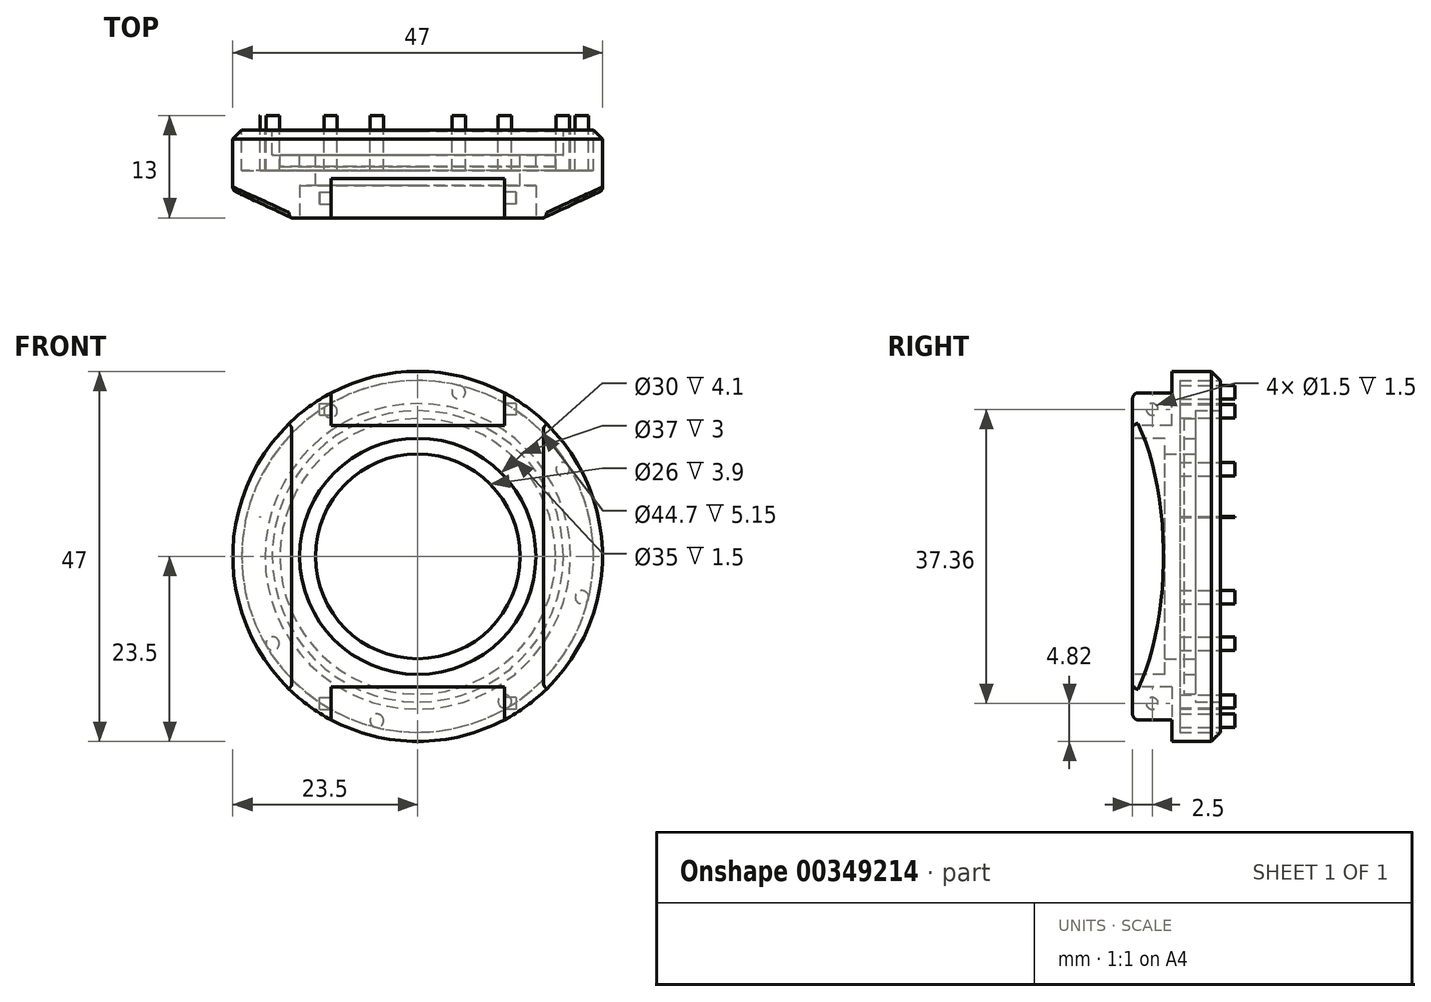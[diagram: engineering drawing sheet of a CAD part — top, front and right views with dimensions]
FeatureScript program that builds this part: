
annotation { "Feature Type Name" : "Feature", "Feature Type Description" : "" }
export const myFeature = defineFeature(function(context is Context, id is Id, definition is map)
    precondition{}
    {
        {
            var Q0;
            Q0=qCreatedBy(makeId("Front.planeOp"),FACE);
            var sketch = newSketch(context, id + "F0", { "sketchPlane" : qUnion([Q0])});
            skCircle(sketch, "E0", {"center": v(0, 0) * mm, "radius": 23.5 * mm});
            skCircle(sketch, "E1", {"center": v(0, 0) * mm, "radius": 15 * mm});
            skLineSegment(sketch, "E2", {"start": v(11, 16.6) * mm, "end": v(11, 20.77) * mm});
            skLineSegment(sketch, "E3", {"start": v(-11, 16.6) * mm, "end": v(11, 16.6) * mm});
            skLineSegment(sketch, "E4.MirrorCS", {"start": v(-11, -16.6) * mm, "end": v(11, -16.6) * mm});
            skLineSegment(sketch, "E5", {"start": v(16, -17.21) * mm, "end": v(16, 17.21) * mm});
            skLineSegment(sketch, "E6.MirrorCS", {"start": v(-16, -17.21) * mm, "end": v(-16, 17.21) * mm});
            skLineSegment(sketch, "E7", {"start": v(-11, -16.6) * mm, "end": v(-11, -20.77) * mm});
            skLineSegment(sketch, "E8", {"start": v(11, -16.6) * mm, "end": v(11, -20.77) * mm});
            skLineSegment(sketch, "E9", {"start": v(-11, 16.6) * mm, "end": v(-11, 20.77) * mm});
            skSolve(sketch);
        }
        {
            var Q0;
            Q0=makeQuery(id+"F0.imprint","IMPRINT",FACE,{"disambiguationData":[TD([[makeQuery(id+"F0.imprint","IMPRINT",EDGE,{"derivedFrom":sQuery(id+"F0.wireOp",EDGE,"E1")}),-1.0]])]});
            var Q1;
            {var subQ0=sQuery(id+"F0.wireOp",EDGE,"E2");Q1=makeQuery(id+"F0.imprint","IMPRINT",FACE,{"disambiguationData":[TD([[makeQuery(id+"F0.imprint","IMPRINT",EDGE,{"derivedFrom":subQ0}),1.0]])]});}
            var Q2;
            {var subQ0=sQuery(id+"F0.wireOp",EDGE,"5be4e37a-e5fa-453b-b9c4-1bad559851300.MirrorCS");Q2=makeQuery(id+"F0.imprint","IMPRINT",FACE,{"disambiguationData":[TD([[makeQuery(id+"F0.imprint","IMPRINT",EDGE,{"derivedFrom":subQ0}),1.0]])]});}
            var Q3;
            {var subQ0=sQuery(id+"F0.wireOp",EDGE,"E6.MirrorCS");Q3=makeQuery(id+"F0.imprint","IMPRINT",FACE,{"disambiguationData":[TD([[makeQuery(id+"F0.imprint","IMPRINT",EDGE,{"derivedFrom":subQ0}),1.0]])]});}
            var Q4;
            {var subQ0=sQuery(id+"F0.wireOp",EDGE,"E5");Q4=makeQuery(id+"F0.imprint","IMPRINT",FACE,{"disambiguationData":[TD([[makeQuery(id+"F0.imprint","IMPRINT",EDGE,{"derivedFrom":subQ0}),-1.0]])]});}
            var Q5;
            Q5=makeQuery(id+"F0.imprint","IMPRINT",FACE,{"disambiguationData":[TD([[makeQuery(id+"F0.imprint","IMPRINT",EDGE,{"derivedFrom":sQuery(id+"F0.wireOp",EDGE,"E1")}),1.0]])]});
            var Q6;
            Q6=makeQuery(id+"F0.imprint","IMPRINT",FACE,{"disambiguationData":[TD([[makeQuery(id+"F0.imprint","IMPRINT",EDGE,{"derivedFrom":sQuery(id+"F0.wireOp",EDGE,"E4.MirrorCS")}),-1.0]])]});
            extrude(context, id + "F1", {"entities" : qUnion([Q0, Q1, Q2, Q3, Q4, Q5, Q6]), "oppositeDirection" : true, "depth" : 13 * mm});
        }
        {
            var Q0;
            {var subQ0=sQuery(id+"F0.wireOp",EDGE,"E2");Q0=makeQuery(id+"F0.imprint","IMPRINT",FACE,{"disambiguationData":[TD([[makeQuery(id+"F0.imprint","IMPRINT",EDGE,{"derivedFrom":subQ0}),1.0]])]});}
            var Q1;
            Q1=makeQuery(id+"F0.imprint","IMPRINT",FACE,{"disambiguationData":[TD([[makeQuery(id+"F0.imprint","IMPRINT",EDGE,{"derivedFrom":sQuery(id+"F0.wireOp",EDGE,"E4.MirrorCS")}),-1.0]])]});
            extrude(context, id + "F2", {"entities" : qUnion([Q0, Q1]), "operationType" : NewBodyOperationType.REMOVE, "oppositeDirection" : true, "depth" : 5 * mm});
        }
        {
            var Q0;
            Q0=makeQuery(id+"F0.imprint","IMPRINT",FACE,{"disambiguationData":[TD([[makeQuery(id+"F0.imprint","IMPRINT",EDGE,{"derivedFrom":sQuery(id+"F0.wireOp",EDGE,"E1")}),1.0]])]});
            extrude(context, id + "F3", {"entities" : qUnion([Q0]), "operationType" : NewBodyOperationType.REMOVE, "oppositeDirection" : true, "depth" : 4.1 * mm});
        }
        {
            var Q0;
            Q0=makeQuery(id+"F1.opExtrude","CAP_FACE",FACE,{"disambiguationData":[OSD([sQuery(id+"F0.wireOp",EDGE,"E0")])],"isStart":false});
            var sketch = newSketch(context, id + "F4", { "sketchPlane" : qUnion([Q0])});
            skCircle(sketch, "E10", {"center": v(0, 0) * mm, "radius": 19.4 * mm});
            skSolve(sketch);
        }
        {
            var Q0;
            Q0=makeQuery(id+"F4.imprint","IMPRINT",FACE,{"disambiguationData":[TD([[makeQuery(id+"F4.imprint","IMPRINT",EDGE,{"derivedFrom":sQuery(id+"F4.wireOp",EDGE,"E10")}),1.0]])]});
            extrude(context, id + "F5", {"entities" : qUnion([Q0]), "operationType" : NewBodyOperationType.REMOVE, "oppositeDirection" : true, "depth" : 2 * mm});
        }
        {
            var Q0;
            Q0=qCreatedBy(makeId("Top.planeOp"),FACE);
            var sketch = newSketch(context, id + "F6", { "sketchPlane" : qUnion([Q0])});
            skLineSegment(sketch, "E11", {"start": v(0, 0) * mm, "end": v(0, 13) * mm});
            skLineSegment(sketch, "E12", {"start": v(16, 0) * mm, "end": v(30.1, 6.57) * mm});
            skLineSegment(sketch, "E13", {"start": v(30.1, 6.57) * mm, "end": v(30.1, 0) * mm});
            skLineSegment(sketch, "E14", {"start": v(30.1, 0) * mm, "end": v(16, 0) * mm});
            skLineSegment(sketch, "E15.MirrorCS", {"start": v(-16, 0) * mm, "end": v(-30.1, 6.57) * mm});
            skLineSegment(sketch, "E16.MirrorCS", {"start": v(-30.1, 0) * mm, "end": v(-16, 0) * mm});
            skLineSegment(sketch, "E17.MirrorCS", {"start": v(-30.1, 6.57) * mm, "end": v(-30.1, 0) * mm});
            skSolve(sketch);
        }
        {
            var Q0;
            Q0=makeQuery(id+"F6.imprint","IMPRINT",FACE,{"disambiguationData":[TD([[makeQuery(id+"F6.imprint","IMPRINT",EDGE,{"derivedFrom":sQuery(id+"F6.wireOp",EDGE,"E15.MirrorCS")}),1.0]])]});
            var Q1;
            Q1=makeQuery(id+"F6.imprint","IMPRINT",FACE,{"disambiguationData":[TD([[makeQuery(id+"F6.imprint","IMPRINT",EDGE,{"derivedFrom":sQuery(id+"F6.wireOp",EDGE,"E12")}),-1.0]])]});
            extrude(context, id + "F7", {"entities" : qUnion([Q0, Q1]), "operationType" : NewBodyOperationType.REMOVE, "oppositeDirection" : true, "depth" : 30 * mm});
        }
        {
            var Q0;
            Q0=makeQuery(id+"F7.boolean.opBoolean","COPY",FACE,{"derivedFrom":makeQuery(id+"F7.opExtrude","CAP_FACE",FACE,{"disambiguationData":[OSD([sQuery(id+"F6.wireOp",EDGE,"E12"),sQuery(id+"F6.wireOp",EDGE,"E13"),sQuery(id+"F6.wireOp",EDGE,"E14")])],"isStart":true})});
            var Q1;
            Q1=makeQuery(id+"F7.boolean.opBoolean","COPY",FACE,{"derivedFrom":makeQuery(id+"F7.opExtrude","CAP_FACE",FACE,{"disambiguationData":[OSD([sQuery(id+"F6.wireOp",EDGE,"E15.MirrorCS"),sQuery(id+"F6.wireOp",EDGE,"E16.MirrorCS"),sQuery(id+"F6.wireOp",EDGE,"E17.MirrorCS")])],"isStart":true})});
            extrude(context, id + "F8", {"entities" : qUnion([Q0, Q1]), "operationType" : NewBodyOperationType.REMOVE, "oppositeDirection" : true, "depth" : 30 * mm});
        }
        {
            var Q0;
            Q0=makeQuery(id+"F8.boolean.opBoolean","INTERSECT",EDGE,{"derivedFrom":[makeQuery(id+"F1.opExtrude","SWEPT_FACE",FACE,{"disambiguationData":[OSD([sQuery(id+"F0.wireOp",EDGE,"E0")])]}),makeQuery(id+"F8.opExtrude","SWEPT_FACE",FACE,{"disambiguationData":[OSD([sQuery(id+"F6.wireOp",EDGE,"E15.MirrorCS")])]})]});
            var Q1;
            {var subQ0=sQuery(id+"F0.wireOp",EDGE,"E0");var subQ2=makeQuery(id+"F2.opExtrude","SWEPT_FACE",FACE,{"disambiguationData":[OSD([sQuery(id+"F0.wireOp",EDGE,"bd44ebf7-4620-4fe3-8905-c25fbdf720250.MirrorCS")])]});Q1=makeQuery(id+"F7.boolean.opBoolean","SPLIT",EDGE,{"disambiguationData":[TD([makeQuery(id+"F2.boolean.opBoolean","COPY",FACE,{"derivedFrom":subQ2})])],"derivedFrom":makeQuery(id+"F2.boolean.opBoolean","SPLIT",EDGE,{"disambiguationData":[TD([subQ2])],"derivedFrom":makeQuery(id+"F1.opExtrude","CAP_EDGE",EDGE,{"disambiguationData":[OSD([subQ0])],"isStart":true})})});}
            var Q2;
            {var subQ0=sQuery(id+"F0.wireOp",EDGE,"E0");var subQ3=makeQuery(id+"F2.opExtrude","SWEPT_FACE",FACE,{"disambiguationData":[OSD([sQuery(id+"F0.wireOp",EDGE,"E2")])]});Q2=makeQuery(id+"F7.boolean.opBoolean","SPLIT",EDGE,{"disambiguationData":[TD([makeQuery(id+"F2.boolean.opBoolean","COPY",FACE,{"derivedFrom":subQ3})])],"derivedFrom":makeQuery(id+"F2.boolean.opBoolean","SPLIT",EDGE,{"disambiguationData":[TD([subQ3])],"derivedFrom":makeQuery(id+"F1.opExtrude","CAP_EDGE",EDGE,{"disambiguationData":[OSD([subQ0])],"isStart":true})})});}
            var Q3;
            Q3=makeQuery(id+"F8.boolean.opBoolean","INTERSECT",EDGE,{"derivedFrom":[makeQuery(id+"F1.opExtrude","SWEPT_FACE",FACE,{"disambiguationData":[OSD([sQuery(id+"F0.wireOp",EDGE,"E0")])]}),makeQuery(id+"F8.opExtrude","SWEPT_FACE",FACE,{"disambiguationData":[OSD([sQuery(id+"F6.wireOp",EDGE,"E12")])]})]});
            var Q4;
            {var subQ0=sQuery(id+"F0.wireOp",EDGE,"E0");var subQ3=makeQuery(id+"F2.opExtrude","SWEPT_FACE",FACE,{"disambiguationData":[OSD([sQuery(id+"F0.wireOp",EDGE,"214ce4b7-124c-478d-bf7d-9a589a4742c70.MirrorCS")])]});Q4=makeQuery(id+"F7.boolean.opBoolean","SPLIT",EDGE,{"disambiguationData":[TD([makeQuery(id+"F2.boolean.opBoolean","COPY",FACE,{"derivedFrom":subQ3})])],"derivedFrom":makeQuery(id+"F2.boolean.opBoolean","SPLIT",EDGE,{"disambiguationData":[TD([makeQuery(id+"F2.opExtrude","SWEPT_FACE",FACE,{"disambiguationData":[OSD([sQuery(id+"F0.wireOp",EDGE,"E2")])]})])],"derivedFrom":makeQuery(id+"F1.opExtrude","CAP_EDGE",EDGE,{"disambiguationData":[OSD([subQ0])],"isStart":true})})});}
            var Q5;
            {var subQ0=sQuery(id+"F0.wireOp",EDGE,"E0");var subQ3=makeQuery(id+"F2.opExtrude","SWEPT_FACE",FACE,{"disambiguationData":[OSD([sQuery(id+"F0.wireOp",EDGE,"5be4e37a-e5fa-453b-b9c4-1bad559851300.MirrorCS")])]});Q5=makeQuery(id+"F7.boolean.opBoolean","SPLIT",EDGE,{"disambiguationData":[TD([makeQuery(id+"F2.boolean.opBoolean","COPY",FACE,{"derivedFrom":subQ3})])],"derivedFrom":makeQuery(id+"F2.boolean.opBoolean","SPLIT",EDGE,{"disambiguationData":[TD([makeQuery(id+"F2.opExtrude","SWEPT_FACE",FACE,{"disambiguationData":[OSD([sQuery(id+"F0.wireOp",EDGE,"bd44ebf7-4620-4fe3-8905-c25fbdf720250.MirrorCS")])]})])],"derivedFrom":makeQuery(id+"F1.opExtrude","CAP_EDGE",EDGE,{"disambiguationData":[OSD([subQ0])],"isStart":true})})});}
            var Q6;
            {var subQ0=sQuery(id+"F0.wireOp",EDGE,"E0");var subQ3=makeQuery(id+"F2.opExtrude","SWEPT_FACE",FACE,{"disambiguationData":[OSD([sQuery(id+"F0.wireOp",EDGE,"5be4e37a-e5fa-453b-b9c4-1bad559851300.MirrorCS")])]});Q6=makeQuery(id+"F7.boolean.opBoolean","SPLIT",EDGE,{"disambiguationData":[TD([makeQuery(id+"F2.boolean.opBoolean","COPY",FACE,{"derivedFrom":subQ3})])],"derivedFrom":makeQuery(id+"F2.boolean.opBoolean","SPLIT",EDGE,{"disambiguationData":[TD([subQ3])],"derivedFrom":makeQuery(id+"F1.opExtrude","CAP_EDGE",EDGE,{"disambiguationData":[OSD([subQ0])],"isStart":true})})});}
            var Q7;
            {var subQ0=sQuery(id+"F0.wireOp",EDGE,"E0");var subQ3=makeQuery(id+"F2.opExtrude","SWEPT_FACE",FACE,{"disambiguationData":[OSD([sQuery(id+"F0.wireOp",EDGE,"b6f2e5ea-f2be-490d-98a8-a135f803b0b40.MirrorCS")])]});Q7=makeQuery(id+"F7.boolean.opBoolean","SPLIT",EDGE,{"disambiguationData":[TD([makeQuery(id+"F2.boolean.opBoolean","COPY",FACE,{"derivedFrom":subQ3})])],"derivedFrom":makeQuery(id+"F2.boolean.opBoolean","SPLIT",EDGE,{"disambiguationData":[TD([makeQuery(id+"F2.opExtrude","SWEPT_FACE",FACE,{"disambiguationData":[OSD([sQuery(id+"F0.wireOp",EDGE,"5be4e37a-e5fa-453b-b9c4-1bad559851300.MirrorCS")])]})])],"derivedFrom":makeQuery(id+"F1.opExtrude","CAP_EDGE",EDGE,{"disambiguationData":[OSD([subQ0])],"isStart":true})})});}
            var Q8;
            {var subQ0=sQuery(id+"F0.wireOp",EDGE,"E0");var subQ3=makeQuery(id+"F2.opExtrude","SWEPT_FACE",FACE,{"disambiguationData":[OSD([sQuery(id+"F0.wireOp",EDGE,"b6f2e5ea-f2be-490d-98a8-a135f803b0b40.MirrorCS")])]});Q8=makeQuery(id+"F7.boolean.opBoolean","SPLIT",EDGE,{"disambiguationData":[TD([makeQuery(id+"F2.boolean.opBoolean","COPY",FACE,{"derivedFrom":subQ3})])],"derivedFrom":makeQuery(id+"F2.boolean.opBoolean","SPLIT",EDGE,{"disambiguationData":[TD([subQ3])],"derivedFrom":makeQuery(id+"F1.opExtrude","CAP_EDGE",EDGE,{"disambiguationData":[OSD([subQ0])],"isStart":true})})});}
            var Q9;
            {var subQ0=sQuery(id+"F0.wireOp",EDGE,"E0");var subQ3=makeQuery(id+"F2.opExtrude","SWEPT_FACE",FACE,{"disambiguationData":[OSD([sQuery(id+"F0.wireOp",EDGE,"E7")])]});Q9=makeQuery(id+"F7.boolean.opBoolean","SPLIT",EDGE,{"disambiguationData":[TD([makeQuery(id+"F2.boolean.opBoolean","COPY",FACE,{"derivedFrom":subQ3})])],"derivedFrom":makeQuery(id+"F2.boolean.opBoolean","SPLIT",EDGE,{"disambiguationData":[TD([makeQuery(id+"F2.opExtrude","SWEPT_FACE",FACE,{"disambiguationData":[OSD([sQuery(id+"F0.wireOp",EDGE,"b6f2e5ea-f2be-490d-98a8-a135f803b0b40.MirrorCS")])]})])],"derivedFrom":makeQuery(id+"F1.opExtrude","CAP_EDGE",EDGE,{"disambiguationData":[OSD([subQ0])],"isStart":true})})});}
            var Q10;
            {var subQ0=sQuery(id+"F0.wireOp",EDGE,"E0");var subQ3=makeQuery(id+"F2.opExtrude","SWEPT_FACE",FACE,{"disambiguationData":[OSD([sQuery(id+"F0.wireOp",EDGE,"E8")])]});Q10=makeQuery(id+"F7.boolean.opBoolean","SPLIT",EDGE,{"disambiguationData":[TD([makeQuery(id+"F2.boolean.opBoolean","COPY",FACE,{"derivedFrom":subQ3})])],"derivedFrom":makeQuery(id+"F2.boolean.opBoolean","SPLIT",EDGE,{"disambiguationData":[TD([makeQuery(id+"F2.opExtrude","SWEPT_FACE",FACE,{"disambiguationData":[OSD([sQuery(id+"F0.wireOp",EDGE,"E2")])]})])],"derivedFrom":makeQuery(id+"F1.opExtrude","CAP_EDGE",EDGE,{"disambiguationData":[OSD([subQ0])],"isStart":true})})});}
            var Q11;
            {var subQ0=sQuery(id+"F0.wireOp",EDGE,"E0");var subQ3=makeQuery(id+"F2.opExtrude","SWEPT_FACE",FACE,{"disambiguationData":[OSD([sQuery(id+"F0.wireOp",EDGE,"E9")])]});Q11=makeQuery(id+"F7.boolean.opBoolean","SPLIT",EDGE,{"disambiguationData":[TD([makeQuery(id+"F2.boolean.opBoolean","COPY",FACE,{"derivedFrom":subQ3})])],"derivedFrom":makeQuery(id+"F2.boolean.opBoolean","SPLIT",EDGE,{"disambiguationData":[TD([makeQuery(id+"F2.opExtrude","SWEPT_FACE",FACE,{"disambiguationData":[OSD([sQuery(id+"F0.wireOp",EDGE,"E7")])]})])],"derivedFrom":makeQuery(id+"F1.opExtrude","CAP_EDGE",EDGE,{"disambiguationData":[OSD([subQ0])],"isStart":true})})});}
            var Q12;
            {var subQ0=sQuery(id+"F0.wireOp",EDGE,"E0");var subQ3=makeQuery(id+"F2.opExtrude","SWEPT_FACE",FACE,{"disambiguationData":[OSD([sQuery(id+"F0.wireOp",EDGE,"E7")])]});Q12=makeQuery(id+"F7.boolean.opBoolean","SPLIT",EDGE,{"disambiguationData":[TD([makeQuery(id+"F2.boolean.opBoolean","COPY",FACE,{"derivedFrom":subQ3})])],"derivedFrom":makeQuery(id+"F2.boolean.opBoolean","SPLIT",EDGE,{"disambiguationData":[TD([subQ3])],"derivedFrom":makeQuery(id+"F1.opExtrude","CAP_EDGE",EDGE,{"disambiguationData":[OSD([subQ0])],"isStart":true})})});}
            fillet(context, id + "F9", {"entities" : qUnion([Q0, Q1, Q2, Q3, Q4, Q5, Q6, Q7, Q8, Q9, Q10, Q11, Q12]), "radius" : 0.7 * mm, "tangentPropagation" : true, "allowEdgeOverflow" : false});
        }
        {
            var Q0;
            Q0=makeQuery(id+"F5.boolean.opBoolean","COPY",FACE,{"derivedFrom":makeQuery(id+"F5.opExtrude","CAP_FACE",FACE,{"disambiguationData":[OSD([sQuery(id+"F4.wireOp",EDGE,"E10")])],"isStart":false})});
            var sketch = newSketch(context, id + "F10", { "sketchPlane" : qUnion([Q0])});
            skCircle(sketch, "E18", {"center": v(0, 0) * mm, "radius": 18.5 * mm});
            skSolve(sketch);
        }
        {
            var Q0;
            Q0=makeQuery(id+"F10.imprint","IMPRINT",FACE,{"disambiguationData":[TD([[makeQuery(id+"F10.imprint","IMPRINT",EDGE,{"derivedFrom":sQuery(id+"F10.wireOp",EDGE,"E18")}),1.0]])]});
            extrude(context, id + "F11", {"entities" : qUnion([Q0]), "operationType" : NewBodyOperationType.REMOVE, "oppositeDirection" : true, "depth" : 3 * mm});
        }
        {
            var Q0;
            Q0=makeQuery(id+"F11.boolean.opBoolean","COPY",FACE,{"derivedFrom":makeQuery(id+"F11.opExtrude","CAP_FACE",FACE,{"disambiguationData":[OSD([sQuery(id+"F10.wireOp",EDGE,"E18")])],"isStart":false})});
            var sketch = newSketch(context, id + "F12", { "sketchPlane" : qUnion([Q0])});
            skCircle(sketch, "E19", {"center": v(0, 0) * mm, "radius": 13 * mm});
            skSolve(sketch);
        }
        {
            var Q0;
            Q0=makeQuery(id+"F12.imprint","IMPRINT",FACE,{"disambiguationData":[TD([[makeQuery(id+"F12.imprint","IMPRINT",EDGE,{"derivedFrom":sQuery(id+"F12.wireOp",EDGE,"E19")}),1.0]])]});
            extrude(context, id + "F13", {"entities" : qUnion([Q0]), "operationType" : NewBodyOperationType.REMOVE, "oppositeDirection" : true, "depth" : 25 * mm});
        }
        {
            var Q0;
            Q0=makeQuery(id+"F1.opExtrude","SWEPT_BODY",BODY,{"disambiguationData":[OSD([sQuery(id+"F0.wireOp",EDGE,"E0")])]});
            transform(context, id + "F14", {"entities" : qUnion([Q0]), "transformType" : TransformType.TRANSLATION_3D, "dx" : 0 * mm, "dy" : 0 * mm, "dz" : 0 * mm, "makeCopy" : true});
        }
        {
            var Q0;
            Q0=makeQuery(id+"F14.opPattern","COPY",BODY,{"derivedFrom":makeQuery(id+"F1.opExtrude","SWEPT_BODY",BODY,{"disambiguationData":[OSD([sQuery(id+"F0.wireOp",EDGE,"E0")])]}),"instanceName":"1"});
            deleteBodies(context, id + "F15", {"entities" : qUnion([Q0])});
        }
        {
            var Q0;
            Q0=makeQuery(id+"F1.opExtrude","CAP_FACE",FACE,{"disambiguationData":[OSD([sQuery(id+"F0.wireOp",EDGE,"E0")])],"isStart":false});
            var sketch = newSketch(context, id + "F16", { "sketchPlane" : qUnion([Q0])});
            skPoint(sketch, "E20.center", {"position": v(0, 0) * mm});
            skCircle(sketch, "E21", {"center": v(0, 0) * mm, "radius": 20.65 * mm});
            skCircle(sketch, "E22", {"center": v(0, 0) * mm, "radius": 22.35 * mm});
            skCircle(sketch, "E23", {"center": v(-20.86, 5.2) * mm, "radius": 0.85 * mm});
            skCircle(sketch, "E24.MirrorC", {"center": v(-20.86, -5.2) * mm, "radius": 0.85 * mm});
            skCircle(sketch, "E25.1.0", {"center": v(-11.07, -18.43) * mm, "radius": 0.85 * mm});
            skCircle(sketch, "E25.1.1", {"center": v(-18.43, -11.07) * mm, "radius": 0.85 * mm});
            skCircle(sketch, "E25.2.0", {"center": v(5.2, -20.86) * mm, "radius": 0.85 * mm});
            skCircle(sketch, "E25.2.1", {"center": v(-5.2, -20.86) * mm, "radius": 0.85 * mm});
            skCircle(sketch, "E26.1.3.0", {"center": v(18.43, -11.07) * mm, "radius": 0.85 * mm});
            skCircle(sketch, "E26.2.3.0", {"center": v(11.07, -18.43) * mm, "radius": 0.85 * mm});
            skCircle(sketch, "E26.1.4.0", {"center": v(20.86, 5.2) * mm, "radius": 0.85 * mm});
            skCircle(sketch, "E26.2.4.0", {"center": v(20.86, -5.2) * mm, "radius": 0.85 * mm});
            skCircle(sketch, "E26.1.5.0", {"center": v(11.07, 18.43) * mm, "radius": 0.85 * mm});
            skCircle(sketch, "E26.2.5.0", {"center": v(18.43, 11.07) * mm, "radius": 0.85 * mm});
            skCircle(sketch, "E26.1.6.0", {"center": v(-5.2, 20.86) * mm, "radius": 0.85 * mm});
            skCircle(sketch, "E26.2.6.0", {"center": v(5.2, 20.86) * mm, "radius": 0.85 * mm});
            skCircle(sketch, "E26.1.7.0", {"center": v(-18.43, 11.07) * mm, "radius": 0.85 * mm});
            skCircle(sketch, "E26.2.7.0", {"center": v(-11.07, 18.43) * mm, "radius": 0.85 * mm});
            skSolve(sketch);
        }
        {
            var Q0;
            {var subQ0=sQuery(id+"F16.wireOp",EDGE,"E20.1.0");var subQ1=makeQuery(id+"F16.imprint","INTERSECT",VERTEX,{"derivedFrom":[subQ0,sQuery(id+"F16.wireOp",EDGE,"E21")]});Q0=makeQuery(id+"F16.imprint","IMPRINT",FACE,{"disambiguationData":[TD([[makeQuery(id+"F16.imprint","IMPRINT",EDGE,{"disambiguationData":[TD([[subQ1,-1.0]])],"derivedFrom":subQ0}),1.0]])]});}
            var Q1;
            {var subQ0=sQuery(id+"F16.wireOp",EDGE,"E21");var subQ6=sQuery(id+"F16.wireOp",EDGE,"E20.1.0");var subQ7=makeQuery(id+"F16.imprint","INTERSECT",VERTEX,{"derivedFrom":[subQ6,subQ0]});Q1=makeQuery(id+"F16.imprint","IMPRINT",FACE,{"disambiguationData":[TD([[makeQuery(id+"F16.imprint","IMPRINT",EDGE,{"disambiguationData":[TD([[subQ7,-1.0]])],"derivedFrom":subQ6}),-1.0]])]});}
            var Q2;
            {var subQ0=sQuery(id+"F16.wireOp",EDGE,"WyNphgvj-kQF1-KeOm-dvJ7-Hw3DE5bhBEOx");var subQ1=sQuery(id+"F16.wireOp",EDGE,"Keh7Dmu7-jVUn-Ag4K-kq0P-PS1Xa7PtDMUz");var subQ2=makeQuery(id+"F16.imprint","INTERSECT",VERTEX,{"derivedFrom":[subQ1,subQ0,sQuery(id+"F16.wireOp",EDGE,"E21")]});Q2=makeQuery(id+"F16.imprint","IMPRINT",FACE,{"disambiguationData":[TD([[makeQuery(id+"F16.imprint","IMPRINT",EDGE,{"disambiguationData":[TD([[subQ2,-1.0]])],"derivedFrom":subQ1}),-1.0]])]});}
            var Q3;
            {var subQ0=sQuery(id+"F16.wireOp",EDGE,"WyNphgvj-kQF1-KeOm-dvJ7-Hw3DE5bhBEOx");var subQ1=sQuery(id+"F16.wireOp",EDGE,"Keh7Dmu7-jVUn-Ag4K-kq0P-PS1Xa7PtDMUz");var subQ2=makeQuery(id+"F16.imprint","INTERSECT",VERTEX,{"derivedFrom":[subQ1,subQ0,sQuery(id+"F16.wireOp",EDGE,"E21")]});Q3=makeQuery(id+"F16.imprint","IMPRINT",FACE,{"disambiguationData":[TD([[makeQuery(id+"F16.imprint","IMPRINT",EDGE,{"disambiguationData":[TD([[subQ2,-1.0]])],"derivedFrom":subQ1}),1.0]])]});}
            var Q4;
            {var subQ0=sQuery(id+"F16.wireOp",EDGE,"E20.23.0");var subQ1=makeQuery(id+"F16.imprint","INTERSECT",VERTEX,{"derivedFrom":[subQ0,sQuery(id+"F16.wireOp",EDGE,"E21")]});Q4=makeQuery(id+"F16.imprint","IMPRINT",FACE,{"disambiguationData":[TD([[makeQuery(id+"F16.imprint","IMPRINT",EDGE,{"disambiguationData":[TD([[subQ1,-1.0]])],"derivedFrom":subQ0}),1.0]])]});}
            var Q5;
            {var subQ0=sQuery(id+"F16.wireOp",EDGE,"E21");var subQ6=sQuery(id+"F16.wireOp",EDGE,"E20.23.0");var subQ7=makeQuery(id+"F16.imprint","INTERSECT",VERTEX,{"derivedFrom":[subQ6,subQ0]});Q5=makeQuery(id+"F16.imprint","IMPRINT",FACE,{"disambiguationData":[TD([[makeQuery(id+"F16.imprint","IMPRINT",EDGE,{"disambiguationData":[TD([[subQ7,1.0]])],"derivedFrom":subQ6}),-1.0]])]});}
            var Q6;
            {var subQ0=sQuery(id+"F16.wireOp",EDGE,"E20.22.0");var subQ1=makeQuery(id+"F16.imprint","INTERSECT",VERTEX,{"derivedFrom":[subQ0,sQuery(id+"F16.wireOp",EDGE,"E21")]});Q6=makeQuery(id+"F16.imprint","IMPRINT",FACE,{"disambiguationData":[TD([[makeQuery(id+"F16.imprint","IMPRINT",EDGE,{"disambiguationData":[TD([[subQ1,-1.0]])],"derivedFrom":subQ0}),1.0]])]});}
            var Q7;
            {var subQ0=sQuery(id+"F16.wireOp",EDGE,"E21");var subQ1=sQuery(id+"F16.wireOp",EDGE,"E20.21.0");var subQ2=makeQuery(id+"F16.imprint","INTERSECT",VERTEX,{"derivedFrom":[subQ1,subQ0]});Q7=makeQuery(id+"F16.imprint","IMPRINT",FACE,{"disambiguationData":[TD([[makeQuery(id+"F16.imprint","IMPRINT",EDGE,{"disambiguationData":[TD([[subQ2,1.0]])],"derivedFrom":subQ1}),-1.0]])]});}
            var Q8;
            {var subQ0=sQuery(id+"F16.wireOp",EDGE,"E20.21.0");var subQ1=makeQuery(id+"F16.imprint","INTERSECT",VERTEX,{"derivedFrom":[subQ0,sQuery(id+"F16.wireOp",EDGE,"E21")]});Q8=makeQuery(id+"F16.imprint","IMPRINT",FACE,{"disambiguationData":[TD([[makeQuery(id+"F16.imprint","IMPRINT",EDGE,{"disambiguationData":[TD([[subQ1,-1.0]])],"derivedFrom":subQ0}),1.0]])]});}
            var Q9;
            {var subQ0=sQuery(id+"F16.wireOp",EDGE,"E21");var subQ1=sQuery(id+"F16.wireOp",EDGE,"E20.20.0");var subQ2=makeQuery(id+"F16.imprint","INTERSECT",VERTEX,{"derivedFrom":[subQ1,subQ0]});Q9=makeQuery(id+"F16.imprint","IMPRINT",FACE,{"disambiguationData":[TD([[makeQuery(id+"F16.imprint","IMPRINT",EDGE,{"disambiguationData":[TD([[subQ2,1.0]])],"derivedFrom":subQ1}),-1.0]])]});}
            var Q10;
            {var subQ0=sQuery(id+"F16.wireOp",EDGE,"E20.20.0");var subQ1=makeQuery(id+"F16.imprint","INTERSECT",VERTEX,{"derivedFrom":[subQ0,sQuery(id+"F16.wireOp",EDGE,"E21")]});Q10=makeQuery(id+"F16.imprint","IMPRINT",FACE,{"disambiguationData":[TD([[makeQuery(id+"F16.imprint","IMPRINT",EDGE,{"disambiguationData":[TD([[subQ1,-1.0]])],"derivedFrom":subQ0}),1.0]])]});}
            var Q11;
            {var subQ0=sQuery(id+"F16.wireOp",EDGE,"E20.19.0");var subQ1=makeQuery(id+"F16.imprint","INTERSECT",VERTEX,{"derivedFrom":[subQ0,sQuery(id+"F16.wireOp",EDGE,"E21")]});Q11=makeQuery(id+"F16.imprint","IMPRINT",FACE,{"disambiguationData":[TD([[makeQuery(id+"F16.imprint","IMPRINT",EDGE,{"disambiguationData":[TD([[subQ1,-1.0]])],"derivedFrom":subQ0}),1.0]])]});}
            var Q12;
            {var subQ0=sQuery(id+"F16.wireOp",EDGE,"E21");var subQ1=sQuery(id+"F16.wireOp",EDGE,"E20.18.0");var subQ2=makeQuery(id+"F16.imprint","INTERSECT",VERTEX,{"derivedFrom":[subQ1,subQ0]});Q12=makeQuery(id+"F16.imprint","IMPRINT",FACE,{"disambiguationData":[TD([[makeQuery(id+"F16.imprint","IMPRINT",EDGE,{"disambiguationData":[TD([[subQ2,1.0]])],"derivedFrom":subQ1}),-1.0]])]});}
            var Q13;
            {var subQ0=sQuery(id+"F16.wireOp",EDGE,"E20.18.0");var subQ1=makeQuery(id+"F16.imprint","INTERSECT",VERTEX,{"derivedFrom":[subQ0,sQuery(id+"F16.wireOp",EDGE,"E21")]});Q13=makeQuery(id+"F16.imprint","IMPRINT",FACE,{"disambiguationData":[TD([[makeQuery(id+"F16.imprint","IMPRINT",EDGE,{"disambiguationData":[TD([[subQ1,-1.0]])],"derivedFrom":subQ0}),1.0]])]});}
            var Q14;
            {var subQ0=sQuery(id+"F16.wireOp",EDGE,"E21");var subQ1=sQuery(id+"F16.wireOp",EDGE,"E20.17.0");var subQ2=makeQuery(id+"F16.imprint","INTERSECT",VERTEX,{"derivedFrom":[subQ1,subQ0]});Q14=makeQuery(id+"F16.imprint","IMPRINT",FACE,{"disambiguationData":[TD([[makeQuery(id+"F16.imprint","IMPRINT",EDGE,{"disambiguationData":[TD([[subQ2,1.0]])],"derivedFrom":subQ1}),-1.0]])]});}
            var Q15;
            {var subQ0=sQuery(id+"F16.wireOp",EDGE,"E20.17.0");var subQ1=makeQuery(id+"F16.imprint","INTERSECT",VERTEX,{"derivedFrom":[subQ0,sQuery(id+"F16.wireOp",EDGE,"E21")]});Q15=makeQuery(id+"F16.imprint","IMPRINT",FACE,{"disambiguationData":[TD([[makeQuery(id+"F16.imprint","IMPRINT",EDGE,{"disambiguationData":[TD([[subQ1,-1.0]])],"derivedFrom":subQ0}),1.0]])]});}
            var Q16;
            {var subQ0=sQuery(id+"F16.wireOp",EDGE,"E20.16.0");var subQ1=makeQuery(id+"F16.imprint","INTERSECT",VERTEX,{"derivedFrom":[subQ0,sQuery(id+"F16.wireOp",EDGE,"E21")]});Q16=makeQuery(id+"F16.imprint","IMPRINT",FACE,{"disambiguationData":[TD([[makeQuery(id+"F16.imprint","IMPRINT",EDGE,{"disambiguationData":[TD([[subQ1,-1.0]])],"derivedFrom":subQ0}),1.0]])]});}
            var Q17;
            {var subQ0=sQuery(id+"F16.wireOp",EDGE,"E21");var subQ1=sQuery(id+"F16.wireOp",EDGE,"E20.15.0");var subQ2=makeQuery(id+"F16.imprint","INTERSECT",VERTEX,{"derivedFrom":[subQ1,subQ0]});Q17=makeQuery(id+"F16.imprint","IMPRINT",FACE,{"disambiguationData":[TD([[makeQuery(id+"F16.imprint","IMPRINT",EDGE,{"disambiguationData":[TD([[subQ2,1.0]])],"derivedFrom":subQ1}),-1.0]])]});}
            var Q18;
            {var subQ0=sQuery(id+"F16.wireOp",EDGE,"E20.15.0");var subQ1=makeQuery(id+"F16.imprint","INTERSECT",VERTEX,{"derivedFrom":[subQ0,sQuery(id+"F16.wireOp",EDGE,"E21")]});Q18=makeQuery(id+"F16.imprint","IMPRINT",FACE,{"disambiguationData":[TD([[makeQuery(id+"F16.imprint","IMPRINT",EDGE,{"disambiguationData":[TD([[subQ1,-1.0]])],"derivedFrom":subQ0}),1.0]])]});}
            var Q19;
            {var subQ0=sQuery(id+"F16.wireOp",EDGE,"E21");var subQ1=sQuery(id+"F16.wireOp",EDGE,"E20.14.0");var subQ2=makeQuery(id+"F16.imprint","INTERSECT",VERTEX,{"derivedFrom":[subQ1,subQ0]});Q19=makeQuery(id+"F16.imprint","IMPRINT",FACE,{"disambiguationData":[TD([[makeQuery(id+"F16.imprint","IMPRINT",EDGE,{"disambiguationData":[TD([[subQ2,1.0]])],"derivedFrom":subQ1}),-1.0]])]});}
            var Q20;
            {var subQ0=sQuery(id+"F16.wireOp",EDGE,"E20.14.0");var subQ1=makeQuery(id+"F16.imprint","INTERSECT",VERTEX,{"derivedFrom":[subQ0,sQuery(id+"F16.wireOp",EDGE,"E21")]});Q20=makeQuery(id+"F16.imprint","IMPRINT",FACE,{"disambiguationData":[TD([[makeQuery(id+"F16.imprint","IMPRINT",EDGE,{"disambiguationData":[TD([[subQ1,-1.0]])],"derivedFrom":subQ0}),1.0]])]});}
            var Q21;
            {var subQ0=sQuery(id+"F16.wireOp",EDGE,"E20.13.0");var subQ1=makeQuery(id+"F16.imprint","INTERSECT",VERTEX,{"derivedFrom":[subQ0,sQuery(id+"F16.wireOp",EDGE,"E21")]});Q21=makeQuery(id+"F16.imprint","IMPRINT",FACE,{"disambiguationData":[TD([[makeQuery(id+"F16.imprint","IMPRINT",EDGE,{"disambiguationData":[TD([[subQ1,-1.0]])],"derivedFrom":subQ0}),1.0]])]});}
            var Q22;
            {var subQ0=sQuery(id+"F16.wireOp",EDGE,"E21");var subQ1=sQuery(id+"F16.wireOp",EDGE,"E20.12.0");var subQ2=makeQuery(id+"F16.imprint","INTERSECT",VERTEX,{"derivedFrom":[subQ1,subQ0]});Q22=makeQuery(id+"F16.imprint","IMPRINT",FACE,{"disambiguationData":[TD([[makeQuery(id+"F16.imprint","IMPRINT",EDGE,{"disambiguationData":[TD([[subQ2,1.0]])],"derivedFrom":subQ1}),-1.0]])]});}
            var Q23;
            {var subQ0=sQuery(id+"F16.wireOp",EDGE,"E20.12.0");var subQ1=makeQuery(id+"F16.imprint","INTERSECT",VERTEX,{"derivedFrom":[subQ0,sQuery(id+"F16.wireOp",EDGE,"E21")]});Q23=makeQuery(id+"F16.imprint","IMPRINT",FACE,{"disambiguationData":[TD([[makeQuery(id+"F16.imprint","IMPRINT",EDGE,{"disambiguationData":[TD([[subQ1,-1.0]])],"derivedFrom":subQ0}),1.0]])]});}
            var Q24;
            {var subQ0=sQuery(id+"F16.wireOp",EDGE,"E21");var subQ1=sQuery(id+"F16.wireOp",EDGE,"E20.11.0");var subQ2=makeQuery(id+"F16.imprint","INTERSECT",VERTEX,{"derivedFrom":[subQ1,subQ0]});Q24=makeQuery(id+"F16.imprint","IMPRINT",FACE,{"disambiguationData":[TD([[makeQuery(id+"F16.imprint","IMPRINT",EDGE,{"disambiguationData":[TD([[subQ2,1.0]])],"derivedFrom":subQ1}),-1.0]])]});}
            var Q25;
            {var subQ0=sQuery(id+"F16.wireOp",EDGE,"E20.11.0");var subQ1=makeQuery(id+"F16.imprint","INTERSECT",VERTEX,{"derivedFrom":[subQ0,sQuery(id+"F16.wireOp",EDGE,"E21")]});Q25=makeQuery(id+"F16.imprint","IMPRINT",FACE,{"disambiguationData":[TD([[makeQuery(id+"F16.imprint","IMPRINT",EDGE,{"disambiguationData":[TD([[subQ1,-1.0]])],"derivedFrom":subQ0}),1.0]])]});}
            var Q26;
            {var subQ0=sQuery(id+"F16.wireOp",EDGE,"E20.10.0");var subQ1=makeQuery(id+"F16.imprint","INTERSECT",VERTEX,{"derivedFrom":[subQ0,sQuery(id+"F16.wireOp",EDGE,"E21")]});Q26=makeQuery(id+"F16.imprint","IMPRINT",FACE,{"disambiguationData":[TD([[makeQuery(id+"F16.imprint","IMPRINT",EDGE,{"disambiguationData":[TD([[subQ1,-1.0]])],"derivedFrom":subQ0}),1.0]])]});}
            var Q27;
            {var subQ0=sQuery(id+"F16.wireOp",EDGE,"E21");var subQ1=sQuery(id+"F16.wireOp",EDGE,"E20.9.0");var subQ2=makeQuery(id+"F16.imprint","INTERSECT",VERTEX,{"derivedFrom":[subQ1,subQ0]});Q27=makeQuery(id+"F16.imprint","IMPRINT",FACE,{"disambiguationData":[TD([[makeQuery(id+"F16.imprint","IMPRINT",EDGE,{"disambiguationData":[TD([[subQ2,1.0]])],"derivedFrom":subQ1}),-1.0]])]});}
            var Q28;
            {var subQ0=sQuery(id+"F16.wireOp",EDGE,"E20.9.0");var subQ1=makeQuery(id+"F16.imprint","INTERSECT",VERTEX,{"derivedFrom":[subQ0,sQuery(id+"F16.wireOp",EDGE,"E21")]});Q28=makeQuery(id+"F16.imprint","IMPRINT",FACE,{"disambiguationData":[TD([[makeQuery(id+"F16.imprint","IMPRINT",EDGE,{"disambiguationData":[TD([[subQ1,-1.0]])],"derivedFrom":subQ0}),1.0]])]});}
            var Q29;
            {var subQ0=sQuery(id+"F16.wireOp",EDGE,"E21");var subQ1=sQuery(id+"F16.wireOp",EDGE,"E20.8.0");var subQ2=makeQuery(id+"F16.imprint","INTERSECT",VERTEX,{"derivedFrom":[subQ1,subQ0]});Q29=makeQuery(id+"F16.imprint","IMPRINT",FACE,{"disambiguationData":[TD([[makeQuery(id+"F16.imprint","IMPRINT",EDGE,{"disambiguationData":[TD([[subQ2,1.0]])],"derivedFrom":subQ1}),-1.0]])]});}
            var Q30;
            {var subQ0=sQuery(id+"F16.wireOp",EDGE,"E20.8.0");var subQ1=makeQuery(id+"F16.imprint","INTERSECT",VERTEX,{"derivedFrom":[subQ0,sQuery(id+"F16.wireOp",EDGE,"E21")]});Q30=makeQuery(id+"F16.imprint","IMPRINT",FACE,{"disambiguationData":[TD([[makeQuery(id+"F16.imprint","IMPRINT",EDGE,{"disambiguationData":[TD([[subQ1,-1.0]])],"derivedFrom":subQ0}),1.0]])]});}
            var Q31;
            {var subQ0=sQuery(id+"F16.wireOp",EDGE,"E20.7.0");var subQ1=makeQuery(id+"F16.imprint","INTERSECT",VERTEX,{"derivedFrom":[subQ0,sQuery(id+"F16.wireOp",EDGE,"E21")]});Q31=makeQuery(id+"F16.imprint","IMPRINT",FACE,{"disambiguationData":[TD([[makeQuery(id+"F16.imprint","IMPRINT",EDGE,{"disambiguationData":[TD([[subQ1,-1.0]])],"derivedFrom":subQ0}),1.0]])]});}
            var Q32;
            {var subQ0=sQuery(id+"F16.wireOp",EDGE,"E21");var subQ1=sQuery(id+"F16.wireOp",EDGE,"E20.6.0");var subQ2=makeQuery(id+"F16.imprint","INTERSECT",VERTEX,{"derivedFrom":[subQ1,subQ0]});Q32=makeQuery(id+"F16.imprint","IMPRINT",FACE,{"disambiguationData":[TD([[makeQuery(id+"F16.imprint","IMPRINT",EDGE,{"disambiguationData":[TD([[subQ2,1.0]])],"derivedFrom":subQ1}),-1.0]])]});}
            var Q33;
            {var subQ0=sQuery(id+"F16.wireOp",EDGE,"E20.6.0");var subQ1=makeQuery(id+"F16.imprint","INTERSECT",VERTEX,{"derivedFrom":[subQ0,sQuery(id+"F16.wireOp",EDGE,"E21")]});Q33=makeQuery(id+"F16.imprint","IMPRINT",FACE,{"disambiguationData":[TD([[makeQuery(id+"F16.imprint","IMPRINT",EDGE,{"disambiguationData":[TD([[subQ1,-1.0]])],"derivedFrom":subQ0}),1.0]])]});}
            var Q34;
            {var subQ0=sQuery(id+"F16.wireOp",EDGE,"E21");var subQ1=sQuery(id+"F16.wireOp",EDGE,"E20.5.0");var subQ2=makeQuery(id+"F16.imprint","INTERSECT",VERTEX,{"derivedFrom":[subQ1,subQ0]});Q34=makeQuery(id+"F16.imprint","IMPRINT",FACE,{"disambiguationData":[TD([[makeQuery(id+"F16.imprint","IMPRINT",EDGE,{"disambiguationData":[TD([[subQ2,1.0]])],"derivedFrom":subQ1}),-1.0]])]});}
            var Q35;
            {var subQ0=sQuery(id+"F16.wireOp",EDGE,"E20.5.0");var subQ1=makeQuery(id+"F16.imprint","INTERSECT",VERTEX,{"derivedFrom":[subQ0,sQuery(id+"F16.wireOp",EDGE,"E21")]});Q35=makeQuery(id+"F16.imprint","IMPRINT",FACE,{"disambiguationData":[TD([[makeQuery(id+"F16.imprint","IMPRINT",EDGE,{"disambiguationData":[TD([[subQ1,-1.0]])],"derivedFrom":subQ0}),1.0]])]});}
            var Q36;
            {var subQ0=sQuery(id+"F16.wireOp",EDGE,"E20.4.0");var subQ1=makeQuery(id+"F16.imprint","INTERSECT",VERTEX,{"derivedFrom":[subQ0,sQuery(id+"F16.wireOp",EDGE,"E21")]});Q36=makeQuery(id+"F16.imprint","IMPRINT",FACE,{"disambiguationData":[TD([[makeQuery(id+"F16.imprint","IMPRINT",EDGE,{"disambiguationData":[TD([[subQ1,-1.0]])],"derivedFrom":subQ0}),1.0]])]});}
            var Q37;
            {var subQ0=sQuery(id+"F16.wireOp",EDGE,"E21");var subQ1=sQuery(id+"F16.wireOp",EDGE,"E20.3.0");var subQ2=makeQuery(id+"F16.imprint","INTERSECT",VERTEX,{"derivedFrom":[subQ1,subQ0]});Q37=makeQuery(id+"F16.imprint","IMPRINT",FACE,{"disambiguationData":[TD([[makeQuery(id+"F16.imprint","IMPRINT",EDGE,{"disambiguationData":[TD([[subQ2,1.0]])],"derivedFrom":subQ1}),-1.0]])]});}
            var Q38;
            {var subQ0=sQuery(id+"F16.wireOp",EDGE,"E20.3.0");var subQ1=makeQuery(id+"F16.imprint","INTERSECT",VERTEX,{"derivedFrom":[subQ0,sQuery(id+"F16.wireOp",EDGE,"E21")]});Q38=makeQuery(id+"F16.imprint","IMPRINT",FACE,{"disambiguationData":[TD([[makeQuery(id+"F16.imprint","IMPRINT",EDGE,{"disambiguationData":[TD([[subQ1,-1.0]])],"derivedFrom":subQ0}),1.0]])]});}
            var Q39;
            {var subQ0=sQuery(id+"F16.wireOp",EDGE,"E21");var subQ1=sQuery(id+"F16.wireOp",EDGE,"E20.2.0");var subQ2=makeQuery(id+"F16.imprint","INTERSECT",VERTEX,{"derivedFrom":[subQ1,subQ0]});Q39=makeQuery(id+"F16.imprint","IMPRINT",FACE,{"disambiguationData":[TD([[makeQuery(id+"F16.imprint","IMPRINT",EDGE,{"disambiguationData":[TD([[subQ2,1.0]])],"derivedFrom":subQ1}),-1.0]])]});}
            var Q40;
            {var subQ0=sQuery(id+"F16.wireOp",EDGE,"E20.2.0");var subQ1=makeQuery(id+"F16.imprint","INTERSECT",VERTEX,{"derivedFrom":[subQ0,sQuery(id+"F16.wireOp",EDGE,"E21")]});Q40=makeQuery(id+"F16.imprint","IMPRINT",FACE,{"disambiguationData":[TD([[makeQuery(id+"F16.imprint","IMPRINT",EDGE,{"disambiguationData":[TD([[subQ1,-1.0]])],"derivedFrom":subQ0}),1.0]])]});}
            var Q41;
            {var subQ0=sQuery(id+"F16.wireOp",EDGE,"E23");var subQ1=makeQuery(id+"F16.imprint","INTERSECT",VERTEX,{"derivedFrom":[sQuery(id+"F16.wireOp",EDGE,"E22"),subQ0]});Q41=makeQuery(id+"F16.imprint","IMPRINT",FACE,{"disambiguationData":[TD([[makeQuery(id+"F16.imprint","IMPRINT",EDGE,{"disambiguationData":[TD([[subQ1,-1.0]])],"derivedFrom":subQ0}),1.0]])]});}
            var Q42;
            {var subQ0=sQuery(id+"F16.wireOp",EDGE,"E24.MirrorC");var subQ1=makeQuery(id+"F16.imprint","INTERSECT",VERTEX,{"derivedFrom":[sQuery(id+"F16.wireOp",EDGE,"E21"),subQ0]});Q42=makeQuery(id+"F16.imprint","IMPRINT",FACE,{"disambiguationData":[TD([[makeQuery(id+"F16.imprint","IMPRINT",EDGE,{"disambiguationData":[TD([[subQ1,1.0]])],"derivedFrom":subQ0}),-1.0]])]});}
            var Q43;
            {var subQ0=sQuery(id+"F16.wireOp",EDGE,"E26.1.7.0");var subQ1=makeQuery(id+"F16.imprint","INTERSECT",VERTEX,{"derivedFrom":[sQuery(id+"F16.wireOp",EDGE,"E21"),subQ0]});Q43=makeQuery(id+"F16.imprint","IMPRINT",FACE,{"disambiguationData":[TD([[makeQuery(id+"F16.imprint","IMPRINT",EDGE,{"disambiguationData":[TD([[subQ1,1.0]])],"derivedFrom":subQ0}),-1.0]])]});}
            var Q44;
            {var subQ0=sQuery(id+"F16.wireOp",EDGE,"E26.2.7.0");var subQ1=sQuery(id+"F16.wireOp",EDGE,"E21");var subQ2=makeQuery(id+"F16.imprint","INTERSECT",VERTEX,{"derivedFrom":[subQ1,subQ0]});Q44=makeQuery(id+"F16.imprint","IMPRINT",FACE,{"disambiguationData":[TD([[makeQuery(id+"F16.imprint","IMPRINT",EDGE,{"disambiguationData":[TD([[subQ2,-1.0]])],"derivedFrom":subQ1}),-1.0]])]});}
            var Q45;
            {var subQ0=sQuery(id+"F16.wireOp",EDGE,"E26.2.7.0");var subQ1=makeQuery(id+"F16.imprint","INTERSECT",VERTEX,{"derivedFrom":[sQuery(id+"F16.wireOp",EDGE,"E21"),subQ0]});Q45=makeQuery(id+"F16.imprint","IMPRINT",FACE,{"disambiguationData":[TD([[makeQuery(id+"F16.imprint","IMPRINT",EDGE,{"disambiguationData":[TD([[subQ1,1.0]])],"derivedFrom":subQ0}),1.0]])]});}
            var Q46;
            {var subQ0=sQuery(id+"F16.wireOp",EDGE,"E26.1.6.0");var subQ1=makeQuery(id+"F16.imprint","INTERSECT",VERTEX,{"derivedFrom":[sQuery(id+"F16.wireOp",EDGE,"E21"),subQ0]});Q46=makeQuery(id+"F16.imprint","IMPRINT",FACE,{"disambiguationData":[TD([[makeQuery(id+"F16.imprint","IMPRINT",EDGE,{"disambiguationData":[TD([[subQ1,1.0]])],"derivedFrom":subQ0}),-1.0]])]});}
            var Q47;
            {var subQ0=sQuery(id+"F16.wireOp",EDGE,"E26.2.6.0");var subQ1=sQuery(id+"F16.wireOp",EDGE,"E21");var subQ2=makeQuery(id+"F16.imprint","INTERSECT",VERTEX,{"derivedFrom":[subQ1,subQ0]});Q47=makeQuery(id+"F16.imprint","IMPRINT",FACE,{"disambiguationData":[TD([[makeQuery(id+"F16.imprint","IMPRINT",EDGE,{"disambiguationData":[TD([[subQ2,-1.0]])],"derivedFrom":subQ1}),-1.0]])]});}
            var Q48;
            {var subQ0=sQuery(id+"F16.wireOp",EDGE,"E26.2.6.0");var subQ1=makeQuery(id+"F16.imprint","INTERSECT",VERTEX,{"derivedFrom":[sQuery(id+"F16.wireOp",EDGE,"E21"),subQ0]});Q48=makeQuery(id+"F16.imprint","IMPRINT",FACE,{"disambiguationData":[TD([[makeQuery(id+"F16.imprint","IMPRINT",EDGE,{"disambiguationData":[TD([[subQ1,1.0]])],"derivedFrom":subQ0}),1.0]])]});}
            var Q49;
            {var subQ0=sQuery(id+"F16.wireOp",EDGE,"E26.1.5.0");var subQ1=makeQuery(id+"F16.imprint","INTERSECT",VERTEX,{"derivedFrom":[sQuery(id+"F16.wireOp",EDGE,"E21"),subQ0]});Q49=makeQuery(id+"F16.imprint","IMPRINT",FACE,{"disambiguationData":[TD([[makeQuery(id+"F16.imprint","IMPRINT",EDGE,{"disambiguationData":[TD([[subQ1,1.0]])],"derivedFrom":subQ0}),-1.0]])]});}
            var Q50;
            {var subQ0=sQuery(id+"F16.wireOp",EDGE,"E26.2.5.0");var subQ1=sQuery(id+"F16.wireOp",EDGE,"E21");var subQ2=makeQuery(id+"F16.imprint","INTERSECT",VERTEX,{"derivedFrom":[subQ1,subQ0]});Q50=makeQuery(id+"F16.imprint","IMPRINT",FACE,{"disambiguationData":[TD([[makeQuery(id+"F16.imprint","IMPRINT",EDGE,{"disambiguationData":[TD([[subQ2,-1.0]])],"derivedFrom":subQ1}),-1.0]])]});}
            var Q51;
            {var subQ0=sQuery(id+"F16.wireOp",EDGE,"E26.2.5.0");var subQ1=makeQuery(id+"F16.imprint","INTERSECT",VERTEX,{"derivedFrom":[sQuery(id+"F16.wireOp",EDGE,"E21"),subQ0]});Q51=makeQuery(id+"F16.imprint","IMPRINT",FACE,{"disambiguationData":[TD([[makeQuery(id+"F16.imprint","IMPRINT",EDGE,{"disambiguationData":[TD([[subQ1,1.0]])],"derivedFrom":subQ0}),1.0]])]});}
            var Q52;
            {var subQ0=sQuery(id+"F16.wireOp",EDGE,"E26.1.4.0");var subQ1=makeQuery(id+"F16.imprint","INTERSECT",VERTEX,{"derivedFrom":[sQuery(id+"F16.wireOp",EDGE,"E21"),subQ0]});Q52=makeQuery(id+"F16.imprint","IMPRINT",FACE,{"disambiguationData":[TD([[makeQuery(id+"F16.imprint","IMPRINT",EDGE,{"disambiguationData":[TD([[subQ1,1.0]])],"derivedFrom":subQ0}),-1.0]])]});}
            var Q53;
            {var subQ0=sQuery(id+"F16.wireOp",EDGE,"E26.1.4.0");var subQ1=sQuery(id+"F16.wireOp",EDGE,"E21");var subQ2=makeQuery(id+"F16.imprint","INTERSECT",VERTEX,{"derivedFrom":[subQ1,subQ0]});Q53=makeQuery(id+"F16.imprint","IMPRINT",FACE,{"disambiguationData":[TD([[makeQuery(id+"F16.imprint","IMPRINT",EDGE,{"disambiguationData":[TD([[subQ2,1.0]])],"derivedFrom":subQ1}),-1.0]])]});}
            var Q54;
            {var subQ0=sQuery(id+"F16.wireOp",EDGE,"E26.2.4.0");var subQ1=makeQuery(id+"F16.imprint","INTERSECT",VERTEX,{"derivedFrom":[sQuery(id+"F16.wireOp",EDGE,"E21"),subQ0]});Q54=makeQuery(id+"F16.imprint","IMPRINT",FACE,{"disambiguationData":[TD([[makeQuery(id+"F16.imprint","IMPRINT",EDGE,{"disambiguationData":[TD([[subQ1,1.0]])],"derivedFrom":subQ0}),1.0]])]});}
            var Q55;
            {var subQ0=sQuery(id+"F16.wireOp",EDGE,"E26.1.3.0");var subQ1=makeQuery(id+"F16.imprint","INTERSECT",VERTEX,{"derivedFrom":[sQuery(id+"F16.wireOp",EDGE,"E21"),subQ0]});Q55=makeQuery(id+"F16.imprint","IMPRINT",FACE,{"disambiguationData":[TD([[makeQuery(id+"F16.imprint","IMPRINT",EDGE,{"disambiguationData":[TD([[subQ1,1.0]])],"derivedFrom":subQ0}),-1.0]])]});}
            var Q56;
            {var subQ0=sQuery(id+"F16.wireOp",EDGE,"E26.2.3.0");var subQ1=sQuery(id+"F16.wireOp",EDGE,"E21");var subQ2=makeQuery(id+"F16.imprint","INTERSECT",VERTEX,{"derivedFrom":[subQ1,subQ0]});Q56=makeQuery(id+"F16.imprint","IMPRINT",FACE,{"disambiguationData":[TD([[makeQuery(id+"F16.imprint","IMPRINT",EDGE,{"disambiguationData":[TD([[subQ2,-1.0]])],"derivedFrom":subQ1}),-1.0]])]});}
            var Q57;
            {var subQ0=sQuery(id+"F16.wireOp",EDGE,"E26.2.3.0");var subQ1=makeQuery(id+"F16.imprint","INTERSECT",VERTEX,{"derivedFrom":[sQuery(id+"F16.wireOp",EDGE,"E21"),subQ0]});Q57=makeQuery(id+"F16.imprint","IMPRINT",FACE,{"disambiguationData":[TD([[makeQuery(id+"F16.imprint","IMPRINT",EDGE,{"disambiguationData":[TD([[subQ1,1.0]])],"derivedFrom":subQ0}),1.0]])]});}
            var Q58;
            {var subQ0=sQuery(id+"F16.wireOp",EDGE,"E25.2.0");var subQ1=makeQuery(id+"F16.imprint","INTERSECT",VERTEX,{"derivedFrom":[sQuery(id+"F16.wireOp",EDGE,"E21"),subQ0]});Q58=makeQuery(id+"F16.imprint","IMPRINT",FACE,{"disambiguationData":[TD([[makeQuery(id+"F16.imprint","IMPRINT",EDGE,{"disambiguationData":[TD([[subQ1,1.0]])],"derivedFrom":subQ0}),-1.0]])]});}
            var Q59;
            {var subQ0=sQuery(id+"F16.wireOp",EDGE,"E25.2.1");var subQ1=sQuery(id+"F16.wireOp",EDGE,"E21");var subQ2=makeQuery(id+"F16.imprint","INTERSECT",VERTEX,{"derivedFrom":[subQ1,subQ0]});Q59=makeQuery(id+"F16.imprint","IMPRINT",FACE,{"disambiguationData":[TD([[makeQuery(id+"F16.imprint","IMPRINT",EDGE,{"disambiguationData":[TD([[subQ2,-1.0]])],"derivedFrom":subQ1}),-1.0]])]});}
            var Q60;
            {var subQ0=sQuery(id+"F16.wireOp",EDGE,"E25.2.1");var subQ1=makeQuery(id+"F16.imprint","INTERSECT",VERTEX,{"derivedFrom":[sQuery(id+"F16.wireOp",EDGE,"E21"),subQ0]});Q60=makeQuery(id+"F16.imprint","IMPRINT",FACE,{"disambiguationData":[TD([[makeQuery(id+"F16.imprint","IMPRINT",EDGE,{"disambiguationData":[TD([[subQ1,1.0]])],"derivedFrom":subQ0}),1.0]])]});}
            var Q61;
            {var subQ0=sQuery(id+"F16.wireOp",EDGE,"E25.1.0");var subQ1=makeQuery(id+"F16.imprint","INTERSECT",VERTEX,{"derivedFrom":[sQuery(id+"F16.wireOp",EDGE,"E21"),subQ0]});Q61=makeQuery(id+"F16.imprint","IMPRINT",FACE,{"disambiguationData":[TD([[makeQuery(id+"F16.imprint","IMPRINT",EDGE,{"disambiguationData":[TD([[subQ1,1.0]])],"derivedFrom":subQ0}),-1.0]])]});}
            var Q62;
            {var subQ0=sQuery(id+"F16.wireOp",EDGE,"E25.1.1");var subQ1=sQuery(id+"F16.wireOp",EDGE,"E21");var subQ2=makeQuery(id+"F16.imprint","INTERSECT",VERTEX,{"derivedFrom":[subQ1,subQ0]});Q62=makeQuery(id+"F16.imprint","IMPRINT",FACE,{"disambiguationData":[TD([[makeQuery(id+"F16.imprint","IMPRINT",EDGE,{"disambiguationData":[TD([[subQ2,-1.0]])],"derivedFrom":subQ1}),-1.0]])]});}
            var Q63;
            {var subQ0=sQuery(id+"F16.wireOp",EDGE,"E25.1.1");var subQ1=makeQuery(id+"F16.imprint","INTERSECT",VERTEX,{"derivedFrom":[sQuery(id+"F16.wireOp",EDGE,"E21"),subQ0]});Q63=makeQuery(id+"F16.imprint","IMPRINT",FACE,{"disambiguationData":[TD([[makeQuery(id+"F16.imprint","IMPRINT",EDGE,{"disambiguationData":[TD([[subQ1,1.0]])],"derivedFrom":subQ0}),1.0]])]});}
            var Q64;
            {var subQ0=sQuery(id+"F16.wireOp",EDGE,"E23");var subQ1=sQuery(id+"F16.wireOp",EDGE,"E21");var subQ2=makeQuery(id+"F16.imprint","INTERSECT",VERTEX,{"derivedFrom":[subQ1,subQ0]});Q64=makeQuery(id+"F16.imprint","IMPRINT",FACE,{"disambiguationData":[TD([[makeQuery(id+"F16.imprint","IMPRINT",EDGE,{"disambiguationData":[TD([[subQ2,-1.0]])],"derivedFrom":subQ1}),-1.0]])]});}
            extrude(context, id + "F17", {"entities" : qUnion([Q0, Q1, Q2, Q3, Q4, Q5, Q6, Q7, Q8, Q9, Q10, Q11, Q12, Q13, Q14, Q15, Q16, Q17, Q18, Q19, Q20, Q21, Q22, Q23, Q24, Q25, Q26, Q27, Q28, Q29, Q30, Q31, Q32, Q33, Q34, Q35, Q36, Q37, Q38, Q39, Q40, Q41, Q42, Q43, Q44, Q45, Q46, Q47, Q48, Q49, Q50, Q51, Q52, Q53, Q54, Q55, Q56, Q57, Q58, Q59, Q60, Q61, Q62, Q63, Q64]), "operationType" : NewBodyOperationType.REMOVE, "oppositeDirection" : true, "depth" : 7 * mm});
        }
        {
            var Q0;
            Q0=makeQuery(id+"F1.opExtrude","CAP_EDGE",EDGE,{"disambiguationData":[OSD([sQuery(id+"F0.wireOp",EDGE,"E0")])],"isStart":false});
            chamfer(context, id + "F18", {"entities" : qUnion([Q0]), "width" : 3 * mm, "tangentPropagation" : true});
        }
        {
            var Q0;
            Q0=makeQuery(id+"F11.boolean.opBoolean","COPY",FACE,{"derivedFrom":makeQuery(id+"F11.opExtrude","CAP_FACE",FACE,{"disambiguationData":[OSD([sQuery(id+"F10.wireOp",EDGE,"E18")])],"isStart":false})});
            var sketch = newSketch(context, id + "F19", { "sketchPlane" : qUnion([Q0])});
            skCircle(sketch, "E27", {"center": v(0, 0) * mm, "radius": 15 * mm});
            skCircle(sketch, "E28", {"center": v(0, 0) * mm, "radius": 17.5 * mm});
            skSolve(sketch);
        }
        {
            var Q0;
            Q0=makeQuery(id+"F19.imprint","IMPRINT",FACE,{"disambiguationData":[TD([[makeQuery(id+"F19.imprint","IMPRINT",EDGE,{"derivedFrom":sQuery(id+"F19.wireOp",EDGE,"E27")}),-1.0]])]});
            extrude(context, id + "F20", {"entities" : qUnion([Q0]), "operationType" : NewBodyOperationType.REMOVE, "oppositeDirection" : true, "depth" : 1.5 * mm});
        }
        {
            var Q0;
            Q0=makeQuery(id+"F2.boolean.opBoolean","COPY",FACE,{"derivedFrom":makeQuery(id+"F2.opExtrude","SWEPT_FACE",FACE,{"disambiguationData":[OSD([sQuery(id+"F0.wireOp",EDGE,"E9")])]})});
            var sketch = newSketch(context, id + "F21", { "sketchPlane" : qUnion([Q0])});
            skLineSegment(sketch, "E29", {"start": v(5, 20.77) * mm, "end": v(0, 16.6) * mm});
            skCircle(sketch, "E30", {"center": v(2.5, 18.68) * mm, "radius": 0.75 * mm});
            skSolve(sketch);
        }
        {
            var Q0;
            {var subQ0=sQuery(id+"F21.wireOp",EDGE,"E30");var subQ1=sQuery(id+"F21.wireOp",EDGE,"E29");var subQ2=makeQuery(id+"F21.imprint","INTERSECT",VERTEX,{"disambiguationData":[OD(0.0)],"derivedFrom":[subQ1,subQ0]});Q0=makeQuery(id+"F21.imprint","IMPRINT",FACE,{"disambiguationData":[TD([[makeQuery(id+"F21.imprint","IMPRINT",EDGE,{"disambiguationData":[TD([[subQ2,-1.0]])],"derivedFrom":subQ1}),-1.0]])]});}
            var Q1;
            {var subQ0=sQuery(id+"F21.wireOp",EDGE,"E30");var subQ1=sQuery(id+"F21.wireOp",EDGE,"E29");var subQ2=makeQuery(id+"F21.imprint","INTERSECT",VERTEX,{"disambiguationData":[OD(0.0)],"derivedFrom":[subQ1,subQ0]});Q1=makeQuery(id+"F21.imprint","IMPRINT",FACE,{"disambiguationData":[TD([[makeQuery(id+"F21.imprint","IMPRINT",EDGE,{"disambiguationData":[TD([[subQ2,-1.0]])],"derivedFrom":subQ1}),1.0]])]});}
            extrude(context, id + "F22", {"entities" : qUnion([Q0, Q1]), "operationType" : NewBodyOperationType.REMOVE, "oppositeDirection" : true, "depth" : 1.5 * mm, "offsetDistance" : 25 * mm});
        }
        {
            var Q0;
            Q0=makeQuery(id+"F2.boolean.opBoolean","COPY",FACE,{"derivedFrom":makeQuery(id+"F2.opExtrude","SWEPT_FACE",FACE,{"disambiguationData":[OSD([sQuery(id+"F0.wireOp",EDGE,"E2")])]})});
            var sketch = newSketch(context, id + "F23", { "sketchPlane" : qUnion([Q0])});
            skLineSegment(sketch, "E31", {"start": v(-5, 20.77) * mm, "end": v(0, 16.6) * mm});
            skCircle(sketch, "E32", {"center": v(-2.5, 18.68) * mm, "radius": 0.75 * mm});
            skSolve(sketch);
        }
        {
            var Q0;
            {var subQ0=sQuery(id+"F23.wireOp",EDGE,"E32");var subQ1=sQuery(id+"F23.wireOp",EDGE,"E31");var subQ2=makeQuery(id+"F23.imprint","INTERSECT",VERTEX,{"disambiguationData":[OD(0.0)],"derivedFrom":[subQ1,subQ0]});Q0=makeQuery(id+"F23.imprint","IMPRINT",FACE,{"disambiguationData":[TD([[makeQuery(id+"F23.imprint","IMPRINT",EDGE,{"disambiguationData":[TD([[subQ2,-1.0]])],"derivedFrom":subQ1}),-1.0]])]});}
            var Q1;
            {var subQ0=sQuery(id+"F23.wireOp",EDGE,"E32");var subQ1=sQuery(id+"F23.wireOp",EDGE,"E31");var subQ2=makeQuery(id+"F23.imprint","INTERSECT",VERTEX,{"disambiguationData":[OD(0.0)],"derivedFrom":[subQ1,subQ0]});Q1=makeQuery(id+"F23.imprint","IMPRINT",FACE,{"disambiguationData":[TD([[makeQuery(id+"F23.imprint","IMPRINT",EDGE,{"disambiguationData":[TD([[subQ2,-1.0]])],"derivedFrom":subQ1}),1.0]])]});}
            var Q2;
            Q2=sQuery(id+"F23.wireOp",EDGE,"E32");
            extrude(context, id + "F24", {"entities" : qUnion([Q0, Q1]), "operationType" : NewBodyOperationType.REMOVE, "surfaceEntities" : qUnion([Q2]), "oppositeDirection" : true, "depth" : 1.5 * mm, "offsetDistance" : 25 * mm});
        }
        {
            var Q0;
            Q0=makeQuery(id+"F2.boolean.opBoolean","COPY",FACE,{"derivedFrom":makeQuery(id+"F2.opExtrude","SWEPT_FACE",FACE,{"disambiguationData":[OSD([sQuery(id+"F0.wireOp",EDGE,"E8")])]})});
            var sketch = newSketch(context, id + "F25", { "sketchPlane" : qUnion([Q0])});
            skLineSegment(sketch, "E33", {"start": v(-5, -20.77) * mm, "end": v(0, -16.6) * mm});
            skCircle(sketch, "E34", {"center": v(-2.5, -18.68) * mm, "radius": 0.75 * mm});
            skSolve(sketch);
        }
        {
            var Q0;
            {var subQ0=sQuery(id+"F25.wireOp",EDGE,"E34");var subQ1=sQuery(id+"F25.wireOp",EDGE,"E33");var subQ2=makeQuery(id+"F25.imprint","INTERSECT",VERTEX,{"disambiguationData":[OD(0.0)],"derivedFrom":[subQ1,subQ0]});Q0=makeQuery(id+"F25.imprint","IMPRINT",FACE,{"disambiguationData":[TD([[makeQuery(id+"F25.imprint","IMPRINT",EDGE,{"disambiguationData":[TD([[subQ2,-1.0]])],"derivedFrom":subQ1}),-1.0]])]});}
            var Q1;
            {var subQ0=sQuery(id+"F25.wireOp",EDGE,"E34");var subQ1=sQuery(id+"F25.wireOp",EDGE,"E33");var subQ2=makeQuery(id+"F25.imprint","INTERSECT",VERTEX,{"disambiguationData":[OD(0.0)],"derivedFrom":[subQ1,subQ0]});Q1=makeQuery(id+"F25.imprint","IMPRINT",FACE,{"disambiguationData":[TD([[makeQuery(id+"F25.imprint","IMPRINT",EDGE,{"disambiguationData":[TD([[subQ2,-1.0]])],"derivedFrom":subQ1}),1.0]])]});}
            var Q2;
            Q2=sQuery(id+"F25.wireOp",EDGE,"E34");
            extrude(context, id + "F26", {"entities" : qUnion([Q0, Q1]), "operationType" : NewBodyOperationType.REMOVE, "surfaceEntities" : qUnion([Q2]), "oppositeDirection" : true, "depth" : 1.5 * mm, "offsetDistance" : 25 * mm});
        }
        {
            var Q0;
            Q0=makeQuery(id+"F2.boolean.opBoolean","COPY",FACE,{"derivedFrom":makeQuery(id+"F2.opExtrude","SWEPT_FACE",FACE,{"disambiguationData":[OSD([sQuery(id+"F0.wireOp",EDGE,"E7")])]})});
            var sketch = newSketch(context, id + "F27", { "sketchPlane" : qUnion([Q0])});
            skLineSegment(sketch, "E35", {"start": v(0, -16.6) * mm, "end": v(5, -20.77) * mm});
            skCircle(sketch, "E36", {"center": v(2.5, -18.68) * mm, "radius": 0.75 * mm});
            skSolve(sketch);
        }
        {
            var Q0;
            Q0 = qSketchRegion(id + "F27", true);
            extrude(context, id + "F28", {"entities" : qUnion([Q0]), "operationType" : NewBodyOperationType.REMOVE, "oppositeDirection" : true, "depth" : 1.5 * mm, "offsetDistance" : 25 * mm});
        }
    });
